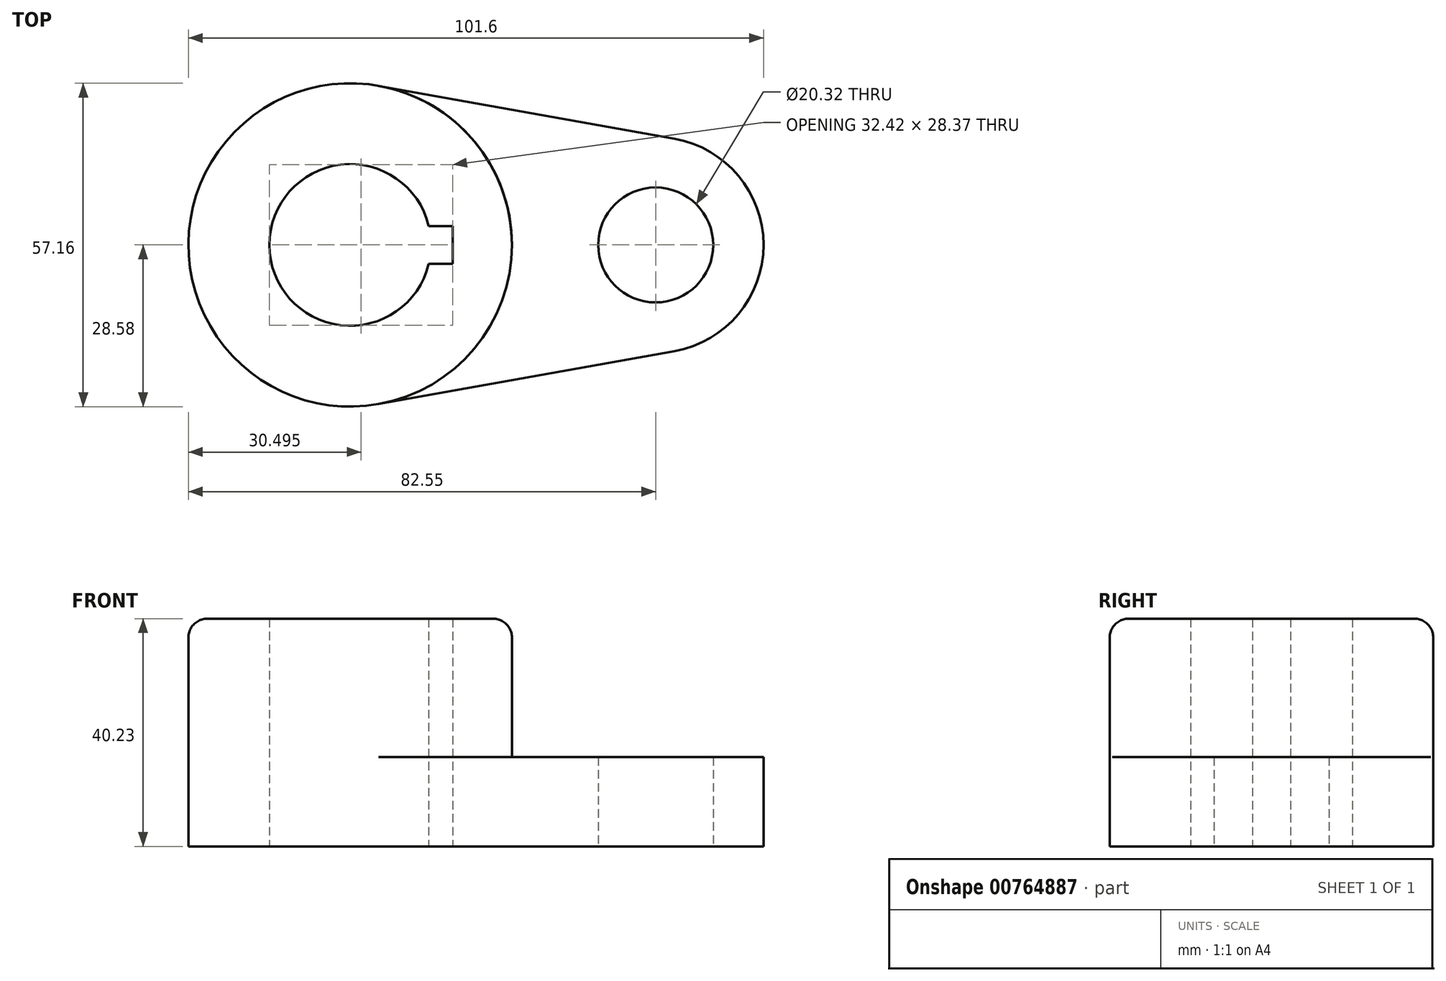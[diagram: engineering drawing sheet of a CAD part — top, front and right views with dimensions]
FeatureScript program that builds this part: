
annotation { "Feature Type Name" : "Feature", "Feature Type Description" : "" }
export const myFeature = defineFeature(function(context is Context, id is Id, definition is map)
    precondition{}
    {
        {
            var Q0;
            Q0=qCreatedBy(makeId("Top.planeOp"),FACE);
            var sketch = newSketch(context, id + "F0", { "sketchPlane" : qUnion([Q0])});
            skLineSegment(sketch, "E0", {"start": v(0, 0) * mm, "end": v(-53.98, 0) * mm});
            skCircle(sketch, "E1", {"center": v(-53.98, 0) * mm, "radius": 28.58 * mm});
            skCircle(sketch, "E2", {"center": v(0, 0) * mm, "radius": 19.05 * mm});
            skCircle(sketch, "E3", {"center": v(0, 0) * mm, "radius": 10.16 * mm});
            skCircle(sketch, "E4", {"center": v(-53.98, 0) * mm, "radius": 14.29 * mm});
            skLineSegment(sketch, "E5", {"start": v(-51.93, 28.66) * mm, "end": v(3.36, 18.75) * mm});
            skLineSegment(sketch, "E6", {"start": v(-48.93, -28.13) * mm, "end": v(3.36, -18.75) * mm});
            skLineSegment(sketch, "E7", {"start": v(-40.09, 3.36) * mm, "end": v(-35.85, 3.36) * mm});
            skLineSegment(sketch, "E8", {"start": v(-35.85, 3.36) * mm, "end": v(-35.85, -3.36) * mm});
            skLineSegment(sketch, "E9", {"start": v(-35.85, -3.36) * mm, "end": v(-40.09, -3.36) * mm});
            skSolve(sketch);
        }
        {
            var Q0;
            Q0=makeQuery(id+"F0.imprint","IMPRINT",FACE,{"disambiguationData":[TD([[makeQuery(id+"F0.imprint","IMPRINT",EDGE,{"derivedFrom":sQuery(id+"F0.wireOp",EDGE,"E3")}),-1.0]])]});
            var Q1;
            {var subQ0=sQuery(id+"F0.wireOp",EDGE,"E1");var subQ1=sQuery(id+"F0.wireOp",EDGE,"E0");var subQ2=makeQuery(id+"F0.imprint","INTERSECT",VERTEX,{"derivedFrom":[subQ1,subQ0]});Q1=makeQuery(id+"F0.imprint","IMPRINT",FACE,{"disambiguationData":[TD([[makeQuery(id+"F0.imprint","IMPRINT",EDGE,{"disambiguationData":[TD([[subQ2,1.0]])],"derivedFrom":subQ1}),-1.0]])]});}
            extrude(context, id + "F1", {"entities" : qUnion([Q0, Q1]), "depth" : 15.77 * mm, "offsetDistance" : 25.4 * mm});
        }
        {
            var Q0;
            {var subQ0=sQuery(id+"F0.wireOp",EDGE,"E7");Q0=makeQuery(id+"F0.imprint","IMPRINT",FACE,{"disambiguationData":[TD([[makeQuery(id+"F0.imprint","IMPRINT",EDGE,{"derivedFrom":subQ0}),1.0]])]});}
            extrude(context, id + "F2", {"entities" : qUnion([Q0]), "operationType" : NewBodyOperationType.ADD, "depth" : 40.23 * mm, "offsetDistance" : 25.4 * mm});
        }
        {
            var Q0;
            {var subQ5=sQuery(id+"F0.wireOp",EDGE,"E6");Q0=makeQuery(id+"F0.imprint","IMPRINT",FACE,{"disambiguationData":[TD([[makeQuery(id+"F0.imprint","IMPRINT",EDGE,{"derivedFrom":subQ5}),1.0]])]});}
            extrude(context, id + "F3", {"entities" : qUnion([Q0]), "operationType" : NewBodyOperationType.ADD, "depth" : 15.77 * mm, "offsetDistance" : 25.4 * mm});
        }
        {
            var Q0;
            Q0=makeQuery(id+"F2.opExtrude","CAP_EDGE",EDGE,{"disambiguationData":[OSD([sQuery(id+"F0.wireOp",EDGE,"E1")])],"isStart":false});
            fillet(context, id + "F4", {"entities" : qUnion([Q0]), "radius" : 3.3 * mm, "tangentPropagation" : true, "allowEdgeOverflow" : false});
        }
    });
